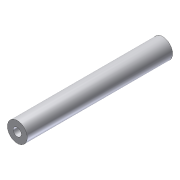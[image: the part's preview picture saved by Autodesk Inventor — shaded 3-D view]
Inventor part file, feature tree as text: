
AUTODESK INVENTOR PART (.ipt)
format: ipt  version: 2012 (Build 160160000, 160)  size: 74,752 bytes
history: native  units: in
note: dims shown in document units (in); Inventor stores cm internally (conversion verified against a paired STEP export)
features: extrude x1, sketch x1
ambient origin geometry x8: Origin, YZ Plane, XZ Plane, XY Plane, X Axis, Y Axis, Z Axis, Center Point
bodies: Solid1 (feature_tree)
feature tree (2):
  extrude  "Extrusion1"  Depth=0.625in
  sketch  "Sketch1"  dims[d0=1.5in d1=0.625in d2=9.5in d3=0.0in]
